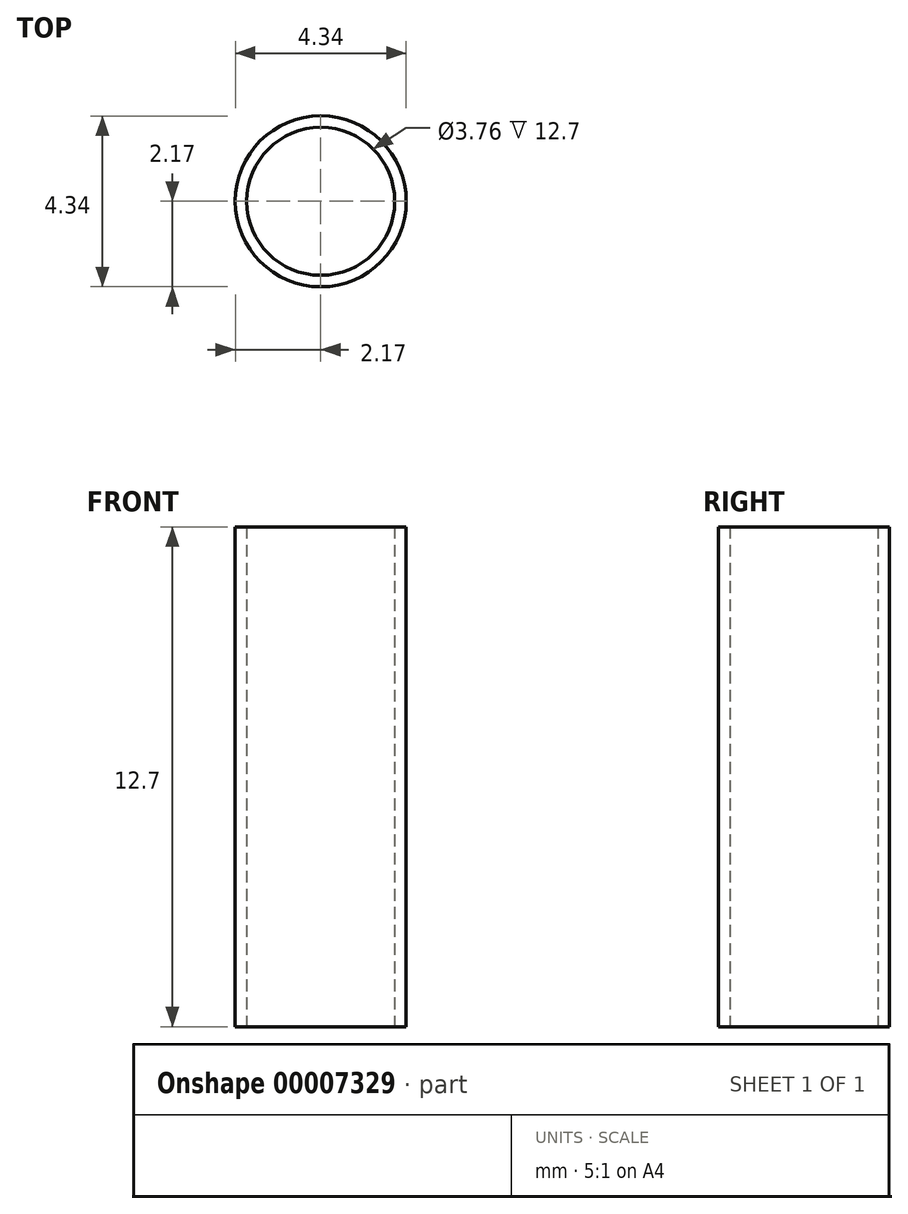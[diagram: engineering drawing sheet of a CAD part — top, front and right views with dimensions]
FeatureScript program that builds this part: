
annotation { "Feature Type Name" : "Feature", "Feature Type Description" : "" }
export const myFeature = defineFeature(function(context is Context, id is Id, definition is map)
    precondition{}
    {
        {
            var Q0;
            Q0=qCreatedBy(makeId("Front.planeOp"),FACE);
            var sketch = newSketch(context, id + "F0", { "sketchPlane" : qUnion([Q0])});
            skLineSegment(sketch, "E0.bottom", {"start": v(1.88, 0) * mm, "end": v(2.17, 0) * mm});
            skLineSegment(sketch, "E0.top", {"start": v(1.88, 12.7) * mm, "end": v(2.17, 12.7) * mm});
            skLineSegment(sketch, "E0.left", {"start": v(1.88, 0) * mm, "end": v(1.88, 12.7) * mm});
            skLineSegment(sketch, "E0.right", {"start": v(2.17, 0) * mm, "end": v(2.17, 12.7) * mm});
            skLineSegment(sketch, "E1", {"start": v(1.88, 0) * mm, "end": v(0, 0) * mm});
            skLineSegment(sketch, "E2", {"start": v(0, 0) * mm, "end": v(0, 12.7) * mm});
            skSolve(sketch);
        }
        {
            var Q0;
            Q0=qSketchRegion(id+"F0",true);
            var Q1;
            Q1=sQuery(id+"F0.wireOp",EDGE,"E2");
            revolve(context, id + "F1", {"entities" : qUnion([Q0]), "axis" : qUnion([Q1]), "revolveType" : RevolveType.FULL});
        }
    });
